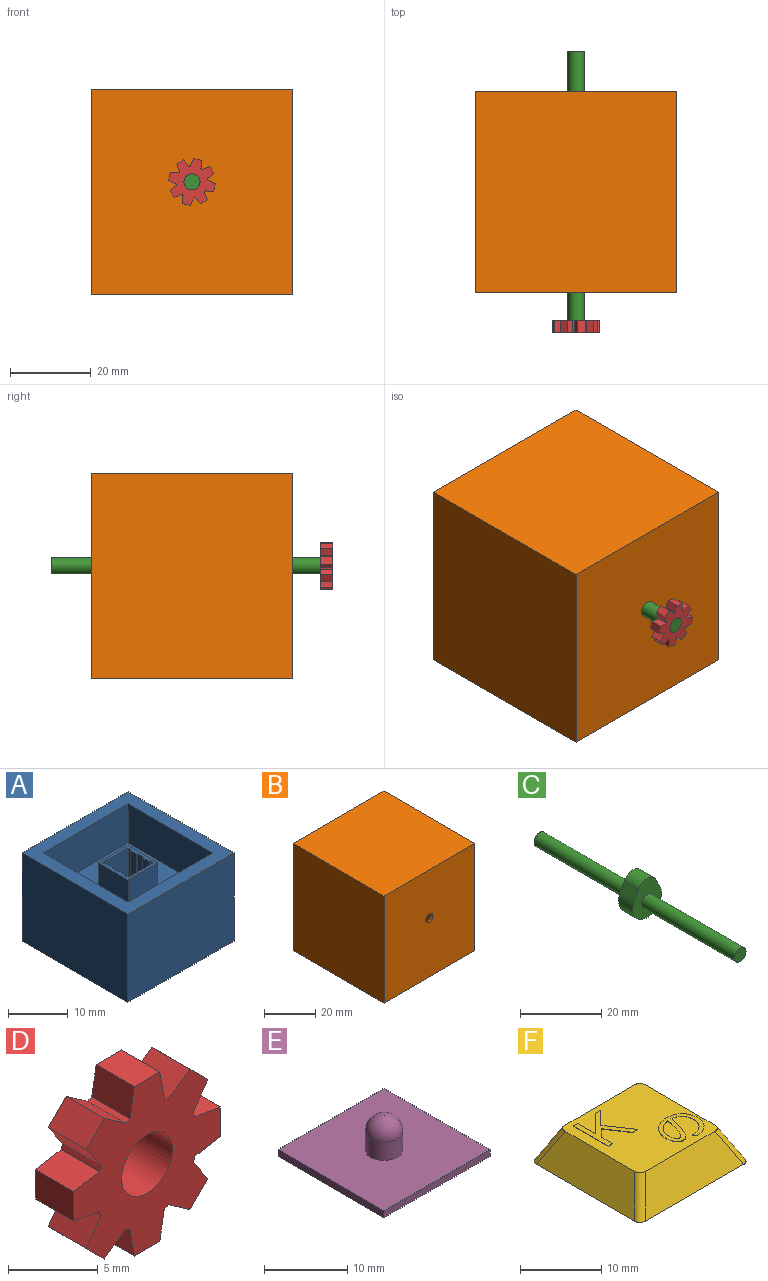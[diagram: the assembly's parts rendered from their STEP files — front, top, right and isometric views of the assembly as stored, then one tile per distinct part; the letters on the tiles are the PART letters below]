
ASSEMBLY  parts=6 mates=6
PART A: 42 faces, bbox 25x25x18 mm
  f0: plane 20x20mm, normal (0,0,1), area 351mm2, adj f1,f2,f3,f4,f32,f33,f34,f35
  f1: plane 7x6mm, normal (0,-1,0), area 42mm2, adj f0,f2,f4,f5
  f2: plane 7x6mm, normal (1,0,0), area 42mm2, adj f0,f1,f3,f5
  f3: plane 7x6mm, normal (0,1,0), area 42mm2, adj f0,f2,f4,f5
  f4: plane 7x6mm, normal (-1,0,0), area 42mm2, adj f0,f1,f3,f5
  f5: plane 7x7mm, normal (0,0,1), area 14.5mm2, adj f1,f2,f3,f4,f6,f7,f8,f9
  f6: plane 7x6mm, normal (0,-1,0), area 42mm2, adj f5,f16,f18,f26
  f7: plane 6x0.25mm, normal (0,-1,0), area 1.5mm2, adj f5,f8,f16,f24
  f8: plane 6x1.5mm, normal (1,0,0), area 9mm2, adj f5,f7,f9,f24
  f9: plane 6x0.25mm, normal (0,1,0), area 1.5mm2, adj f5,f8,f16,f24
  f10: plane 6x0.25mm, normal (0,1,0), area 1.5mm2, adj f5,f11,f18,f23
  f11: plane 6x1.5mm, normal (-1,0,0), area 9mm2, adj f5,f10,f12,f23
  f12: plane 6x0.25mm, normal (0,-1,0), area 1.5mm2, adj f5,f11,f18,f23
  f13: plane 6x0.25mm, normal (0,-1,0), area 1.5mm2, adj f5,f14,f16,f22
  f14: plane 6x1.5mm, normal (1,0,0), area 9mm2, adj f5,f13,f15,f22
  f15: plane 6x0.25mm, normal (0,1,0), area 1.5mm2, adj f5,f14,f16,f22
  f16: plane 7x6mm, normal (1,0,0), area 24mm2, adj f5,f6,f7,f9,f13,f15,f17,f22
  f17: plane 7x6mm, normal (0,1,0), area 42mm2, adj f5,f16,f18,f26
  f18: plane 7x6mm, normal (-1,0,0), area 24mm2, adj f5,f6,f10,f12,f17,f19,f21,f23
  f19: plane 6x0.25mm, normal (0,1,0), area 1.5mm2, adj f5,f18,f20,f25
  f20: plane 6x1.5mm, normal (-1,0,0), area 9mm2, adj f5,f19,f21,f25
  f21: plane 6x0.25mm, normal (0,-1,0), area 1.5mm2, adj f5,f18,f20,f25
  f22: plane 1.5x0.25mm, normal (0,0,-1), area 0.4mm2, adj f13,f14,f15,f16
  f23: plane 1.5x0.25mm, normal (0,0,-1), area 0.4mm2, adj f10,f11,f12,f18
  f24: plane 1.5x0.25mm, normal (0,0,-1), area 0.4mm2, adj f7,f8,f9,f16
  f25: plane 1.5x0.25mm, normal (0,0,-1), area 0.4mm2, adj f18,f19,f20,f21
  f26: plane 20x20mm, normal (0,0,-1), area 364mm2, adj f6,f16,f17,f18,f27,f28,f29,f30
  f27: plane 20x5mm, normal (0,-1,0), area 100mm2, adj f26,f28,f30,f31
  f28: plane 20x5mm, normal (-1,0,0), area 100mm2, adj f26,f27,f29,f31
  f29: plane 20x5mm, normal (0,1,0), area 100mm2, adj f26,f28,f30,f31
  f30: plane 20x5mm, normal (1,0,0), area 100mm2, adj f26,f27,f29,f31
  f31: plane 20x20mm, normal (0,0,1), area 400mm2, adj f27,f28,f29,f30
  f32: plane 20x8mm, normal (-1,0,0), area 160mm2, adj f0,f33,f35,f36
  f33: plane 20x8mm, normal (0,1,0), area 160mm2, adj f0,f32,f34,f36
  f34: plane 20x8mm, normal (1,0,0), area 160mm2, adj f0,f33,f35,f36
  f35: plane 20x8mm, normal (0,-1,0), area 160mm2, adj f0,f32,f34,f36
  f36: plane 25x25mm, normal (0,0,1), area 225mm2, adj f32,f33,f34,f35,f38,f39,f40,f41
  f37: plane 25x25mm, normal (0,0,-1), area 625mm2, adj f38,f39,f40,f41
  f38: plane 25x18mm, normal (-1,0,0), area 450mm2, adj f36,f37,f39,f41
  f39: plane 25x18mm, normal (0,1,0), area 450mm2, adj f36,f37,f38,f40
  f40: plane 25x18mm, normal (1,0,0), area 450mm2, adj f36,f37,f39,f41
  f41: plane 25x18mm, normal (0,-1,0), area 450mm2, adj f36,f37,f38,f40
PART B: 14 faces, bbox 50x50x51 mm
  f0: plane 51x50mm, normal (0,-1,0), area 2537.4mm2, adj f1,f3,f4,f11,f13
  f1: plane 51x50mm, normal (1,0,0), area 2550mm2, adj f0,f2,f4,f13
  f2: plane 51x50mm, normal (0,1,0), area 2537.4mm2, adj f1,f3,f4,f10,f13
  f3: plane 51x50mm, normal (-1,0,0), area 2550mm2, adj f0,f2,f4,f13
  f4: plane 50x50mm, normal (0,0,-1), area 2500mm2, adj f0,f1,f2,f3
  f5: plane 49x48mm, normal (0,1,0), area 2339.4mm2, adj f6,f8,f9,f11,f12
  f6: plane 49x48mm, normal (-1,0,0), area 2352mm2, adj f5,f7,f9,f12
  f7: plane 49x48mm, normal (0,-1,0), area 2339.4mm2, adj f6,f8,f9,f10,f12
  f8: plane 49x48mm, normal (1,0,0), area 2352mm2, adj f5,f7,f9,f12
  f9: plane 48x48mm, normal (0,0,1), area 2304mm2, adj f5,f6,f7,f8
  f10: cylinder r=2mm len=4mm, axis (0,-1,0), area 12.6mm2, adj f2,f7
  f11: cylinder r=2mm len=4mm, axis (0,-1,0), area 12.6mm2, adj f0,f5
  f12: plane 48x48mm, normal (0,0,-1), area 2304mm2, adj f5,f6,f7,f8
  f13: plane 50x50mm, normal (0,0,1), area 2500mm2, adj f0,f1,f2,f3
PART C: 10 faces, bbox 10x70x11.9 mm
  f0: plane 5x2.79mm, normal (0.89,0,0.45), area 15.6mm2, adj f1,f3,f4,f5
  f1: cylinder r=3.43mm len=6.12mm, axis (0,1,0), area 37.8mm2, adj f0,f2,f4,f5
  f2: plane 5x2.79mm, normal (-0.89,0,0.45), area 15.6mm2, adj f1,f3,f4,f5
  f3: cylinder r=5mm len=10mm, axis (0,1,0), area 101.9mm2, adj f0,f2,f4,f5
  f4: plane 11.93x10mm, normal (0,-1,0), area 77.7mm2, adj f0,f1,f2,f3,f8
  f5: plane 11.93x10mm, normal (0,1,0), area 77.7mm2, adj f0,f1,f2,f3,f7
  f6: plane 4x4mm, normal (0,1,0), area 12.6mm2, adj f7
  f7: cylinder r=2mm len=32.5mm, axis (0,1,0), area 408.4mm2, adj f5,f6
  f8: cylinder r=2mm len=32.5mm, axis (0,1,0), area 408.4mm2, adj f4,f9
  f9: plane 4x4mm, normal (0,-1,0), area 12.6mm2, adj f8
PART D: 35 faces, bbox 11.5x3x11.5 mm
  f0: plane 3x1.66mm, normal (-0.57,0,0.82), area 6.1mm2, adj f1,f31,f33,f34
  f1: cylinder r=4mm len=3mm, axis (0,-1,0), area 1.1mm2, adj f0,f2,f33,f34
  f2: plane 3x2mm, normal (0.98,0,0.17), area 6.1mm2, adj f1,f3,f33,f34
  f3: plane 3x2mm, normal (0,0,1), area 6mm2, adj f2,f4,f33,f34
  f4: plane 3x2mm, normal (-0.98,0,0.17), area 6.1mm2, adj f3,f5,f33,f34
  f5: cylinder r=4mm len=3mm, axis (0,-1,0), area 1.1mm2, adj f4,f6,f33,f34
  f6: plane 3x1.66mm, normal (0.57,0,0.82), area 6.1mm2, adj f5,f7,f33,f34
  f7: plane 3x1.41mm, normal (-0.71,0,0.71), area 6mm2, adj f6,f8,f33,f34
  f8: plane 3x1.66mm, normal (-0.82,0,-0.57), area 6.1mm2, adj f7,f9,f33,f34
  f9: cylinder r=4mm len=3mm, axis (0,-1,0), area 1.1mm2, adj f8,f10,f33,f34
  f10: plane 3x2mm, normal (-0.17,0,0.98), area 6.1mm2, adj f9,f11,f33,f34
  f11: plane 3x2mm, normal (-1,0,0), area 6mm2, adj f10,f12,f33,f34
  f12: plane 3x2mm, normal (-0.17,0,-0.98), area 6.1mm2, adj f11,f13,f33,f34
  f13: cylinder r=4mm len=3mm, axis (0,-1,0), area 1.1mm2, adj f12,f14,f33,f34
  f14: plane 3x1.66mm, normal (-0.82,0,0.57), area 6.1mm2, adj f13,f15,f33,f34
  f15: plane 3x1.41mm, normal (-0.71,0,-0.71), area 6mm2, adj f14,f16,f33,f34
  f16: plane 3x1.66mm, normal (0.57,0,-0.82), area 6.1mm2, adj f15,f17,f33,f34
  f17: cylinder r=4mm len=3mm, axis (0,-1,0), area 1.1mm2, adj f16,f18,f33,f34
  f18: plane 3x2mm, normal (-0.98,0,-0.17), area 6.1mm2, adj f17,f19,f33,f34
  f19: plane 3x2mm, normal (0,0,-1), area 6mm2, adj f18,f20,f33,f34
  f20: plane 3x2mm, normal (0.98,0,-0.17), area 6.1mm2, adj f19,f21,f33,f34
  f21: cylinder r=4mm len=3mm, axis (0,-1,0), area 1.1mm2, adj f20,f22,f33,f34
  f22: plane 3x1.66mm, normal (-0.57,0,-0.82), area 6.1mm2, adj f21,f23,f33,f34
  f23: plane 3x1.41mm, normal (0.71,0,-0.71), area 6mm2, adj f22,f24,f33,f34
  f24: plane 3x1.66mm, normal (0.82,0,0.57), area 6.1mm2, adj f23,f25,f33,f34
  f25: cylinder r=4mm len=3mm, axis (0,-1,0), area 1.1mm2, adj f24,f26,f33,f34
  f26: plane 3x2mm, normal (0.17,0,-0.98), area 6.1mm2, adj f25,f27,f33,f34
  f27: plane 3x2mm, normal (1,0,0), area 6mm2, adj f26,f28,f33,f34
  f28: plane 3x2mm, normal (0.17,0,0.98), area 6.1mm2, adj f27,f29,f33,f34
  f29: cylinder r=4mm len=3mm, axis (0,-1,0), area 1.1mm2, adj f28,f30,f33,f34
  f30: plane 3x1.66mm, normal (0.82,0,-0.57), area 6.1mm2, adj f29,f31,f33,f34
  f31: plane 3x1.41mm, normal (0.71,0,0.71), area 6mm2, adj f0,f30,f33,f34
  f32: cylinder r=2mm len=4mm, axis (0,-1,0), area 37.7mm2, adj f33,f34
  f33: plane 11.53x11.53mm, normal (0,1,0), area 71.9mm2, adj f0,f1,f2,f3,f4,f5,f6,f7
  f34: plane 11.53x11.53mm, normal (0,-1,0), area 71.9mm2, adj f0,f1,f2,f3,f4,f5,f6,f7
PART E: 8 faces, bbox 18x18x6 mm
  f0: cylinder r=2.25mm len=4.5mm, axis (0,0,-1), area 38.9mm2, adj f1,f7
  f1: sphere r=2.25mm, area 31.8mm2, adj f0
  f2: plane 18x1mm, normal (1,0,0), area 18mm2, adj f3,f5,f6,f7
  f3: plane 18x1mm, normal (0,1,0), area 18mm2, adj f2,f4,f6,f7
  f4: plane 18x1mm, normal (-1,0,0), area 18mm2, adj f3,f5,f6,f7
  f5: plane 18x1mm, normal (0,-1,0), area 18mm2, adj f2,f4,f6,f7
  f6: plane 18x18mm, normal (0,0,-1), area 324mm2, adj f2,f3,f4,f5
  f7: plane 18x18mm, normal (0,0,1), area 308.1mm2, adj f0,f2,f3,f4,f5
PART F: 76 faces, bbox 19.1x19.1x10.1 mm
  f0: plane 14x14mm, normal (0,0,1), area 168.2mm2, adj f7,f8,f9,f10,f42,f43,f44,f45
  f1: plane 9.5x1.5mm, normal (1,0,0), area 14.2mm2, adj f5,f11,f33,f38
  f2: plane 9.5x0.75mm, normal (1,0,0), area 7.1mm2, adj f5,f11,f16,f35
  f3: plane 9.5x0.75mm, normal (-1,0,0), area 7.1mm2, adj f5,f11,f16,f39
  f4: plane 9.5x1.5mm, normal (-1,0,0), area 14.2mm2, adj f5,f11,f30,f41
  f5: plane 6x6mm, normal (0,0,-1), area 12mm2, adj f1,f2,f3,f4,f16,f17,f18,f19
  f6: plane 19x19mm, normal (0,0,-1), area 40.6mm2, adj f7,f8,f9,f10,f12,f13,f14,f15
  f7: plane 17.21x5mm, normal (0,0.89,0.45), area 82.2mm2, adj f0,f6,f44,f45
  f8: plane 17.21x5mm, normal (-0.89,0,0.45), area 82.2mm2, adj f0,f6,f43,f44
  f9: plane 17.21x5mm, normal (0,-0.89,0.45), area 82.2mm2, adj f0,f6,f42,f43
  f10: plane 17.21x5mm, normal (0.89,0,0.45), area 82.2mm2, adj f0,f6,f42,f45
  f11: plane 13.38x13.38mm, normal (0,0,-1), area 144.6mm2, adj f1,f2,f3,f4,f12,f13,f14,f15
  f12: plane 17.88x4.5mm, normal (0,-0.89,-0.45), area 78.6mm2, adj f6,f11,f13,f15
  f13: plane 17.88x4.5mm, normal (0.89,0,-0.45), area 78.6mm2, adj f6,f11,f12,f14
  f14: plane 17.88x4.5mm, normal (0,0.89,-0.45), area 78.6mm2, adj f6,f11,f13,f15
  f15: plane 17.88x4.5mm, normal (-0.89,0,-0.45), area 78.6mm2, adj f6,f11,f12,f14
  f16: plane 9.5x6mm, normal (0,1,0), area 57mm2, adj f2,f3,f5,f11
  f17: plane 9.5x0.75mm, normal (1,0,0), area 7.1mm2, adj f5,f11,f18,f36
  f18: plane 9.5x6mm, normal (0,-1,0), area 57mm2, adj f5,f11,f17,f19
  f19: plane 9.5x0.75mm, normal (-1,0,0), area 7.1mm2, adj f5,f11,f18,f32
  f20: plane 9.5x2.25mm, normal (0,-1,0), area 21.4mm2, adj f5,f21,f23,f24
  f21: plane 9.5x5mm, normal (-1,0,0), area 47.5mm2, adj f5,f20,f22,f24
  f22: plane 9.5x2.25mm, normal (0,1,0), area 21.4mm2, adj f5,f21,f23,f24
  f23: plane 9.5x5mm, normal (1,0,0), area 47.5mm2, adj f5,f20,f22,f24
  f24: plane 5x2.25mm, normal (0,0,-1), area 11.2mm2, adj f20,f21,f22,f23
  f25: plane 9.5x5mm, normal (1,0,0), area 47.5mm2, adj f5,f26,f28,f29
  f26: plane 9.5x2.25mm, normal (0,-1,0), area 21.4mm2, adj f5,f25,f27,f29
  f27: plane 9.5x5mm, normal (-1,0,0), area 47.5mm2, adj f5,f26,f28,f29
  f28: plane 9.5x2.25mm, normal (0,1,0), area 21.4mm2, adj f5,f25,f27,f29
  f29: plane 5x2.25mm, normal (0,0,-1), area 11.2mm2, adj f25,f26,f27,f28
  f30: plane 9.5x0.25mm, normal (0,-1,0), area 2.4mm2, adj f4,f5,f11,f31
  f31: plane 9.5x1.5mm, normal (-1,0,0), area 14.2mm2, adj f5,f11,f30,f32
  f32: plane 9.5x0.25mm, normal (0,1,0), area 2.4mm2, adj f5,f11,f19,f31
  f33: plane 9.5x0.25mm, normal (0,1,0), area 2.4mm2, adj f1,f5,f11,f34
  f34: plane 9.5x1.5mm, normal (1,0,0), area 14.2mm2, adj f5,f11,f33,f35
  f35: plane 9.5x0.25mm, normal (0,-1,0), area 2.4mm2, adj f2,f5,f11,f34
  f36: plane 9.5x0.25mm, normal (0,1,0), area 2.4mm2, adj f5,f11,f17,f37
  f37: plane 9.5x1.5mm, normal (1,0,0), area 14.2mm2, adj f5,f11,f36,f38
  f38: plane 9.5x0.25mm, normal (0,-1,0), area 2.4mm2, adj f1,f5,f11,f37
  f39: plane 9.5x0.25mm, normal (0,-1,0), area 2.4mm2, adj f3,f5,f11,f40
  f40: plane 9.5x1.5mm, normal (-1,0,0), area 14.2mm2, adj f5,f11,f39,f41
  f41: plane 9.5x0.25mm, normal (0,1,0), area 2.4mm2, adj f4,f5,f11,f40
  f42: cylinder r=1mm len=5.26mm, axis (-0.41,0.41,0.82), area 8.4mm2, adj f0,f6,f9,f10
  f43: cylinder r=1mm len=5.26mm, axis (-0.41,-0.41,-0.82), area 8.4mm2, adj f0,f6,f8,f9
  f44: cylinder r=1mm len=5.26mm, axis (0.41,-0.41,0.82), area 8.4mm2, adj f0,f6,f7,f8
  f45: cylinder r=1mm len=5.26mm, axis (0.41,0.41,-0.82), area 8.4mm2, adj f0,f6,f7,f10
  f46: plane 6.13x0.05mm, normal (-1,0,0), area 0.3mm2, adj f0,f47,f50,f59
  f47: plane 0.77x0.05mm, normal (0,-1,0), area 0mm2, adj f0,f46,f51,f59
  f48: plane 0.88x0.05mm, normal (0,-1,0), area 0mm2, adj f0,f53,f54,f59
  f49: plane 0.89x0.05mm, normal (0,1,0), area 0mm2, adj f0,f55,f56,f59
  f50: plane 0.77x0.05mm, normal (0,1,0), area 0mm2, adj f0,f46,f58,f59
  f51: plane 1.92x0.05mm, normal (1,0,0), area 0.1mm2, adj f0,f47,f52,f59
  f52: plane 1.32x1.28mm, normal (0.72,-0.7,0), area 0.1mm2, adj f0,f51,f53,f59
  f53: plane 3.23x2.16mm, normal (-0.83,-0.56,0), area 0.2mm2, adj f0,f48,f52,f59
  f54: plane 3.78x2.56mm, normal (0.83,0.56,0), area 0.2mm2, adj f0,f48,f55,f59
  f55: plane 2.34x2.22mm, normal (0.73,-0.69,0), area 0.2mm2, adj f0,f49,f54,f59
  f56: plane 3.14x3.05mm, normal (-0.72,0.7,0), area 0.2mm2, adj f0,f49,f57,f59
  f57: plane 0.05x0.03mm, normal (0,1,0), area 0mm2, adj f0,f56,f58,f59
  f58: plane 3.14x0.05mm, normal (1,0,0), area 0.2mm2, adj f0,f50,f57,f59
  f59: plane 6.13x5.08mm, normal (0,0,1), area 11.2mm2, adj f46,f47,f48,f49,f50,f51,f52,f53
  f60: extruded ~2.77x2.65mm, area 0.2mm2, adj f0,f61,f68,f74
  f61: extruded ~3.16x2.94mm, area 0.2mm2, adj f0,f60,f62,f74
  f62: extruded ~1.93x1.29mm, area 0.1mm2, adj f0,f61,f63,f74
  f63: extruded ~2.24x1.69mm, area 0.1mm2, adj f0,f62,f69,f74
  f64: extruded ~1.7x1.09mm, area 0.1mm2, adj f65,f73,f74,f75
  f65: extruded ~1.31x0.74mm, area 0.1mm2, adj f64,f66,f74,f75
  f66: extruded ~2.33x2.23mm, area 0.2mm2, adj f65,f73,f74,f75
  f67: plane 0.55x0.34mm, normal (-0.85,-0.52,0), area 0mm2, adj f0,f68,f72,f74
  f68: extruded ~2.75x2.72mm, area 0.2mm2, adj f0,f60,f67,f74
  f69: extruded ~2.08x0.43mm, area 0.1mm2, adj f0,f63,f70,f74
  f70: extruded ~2.09x1.92mm, area 0.2mm2, adj f0,f69,f71,f74
  f71: extruded ~2.14x1.83mm, area 0.2mm2, adj f0,f70,f72,f74
  f72: extruded ~0.62x0.09mm, area 0mm2, adj f0,f67,f71,f74
  f73: extruded ~1.95x0.4mm, area 0.1mm2, adj f64,f66,f74,f75
  f74: plane 5.93x5.4mm, normal (0,0,1), area 11mm2, adj f60,f61,f62,f63,f64,f65,f66,f67
  f75: plane 3.64x2.23mm, normal (0,0,1), area 5mm2, adj f64,f65,f66,f73
PLACE A rot(axis=(-0.01,0.7,-0.71),0deg) t=(-37.27,-50.85,-43.99)mm
PLACE B t=(-37.27,-50.85,-43.99)mm fixed
PLACE C rot(axis=(0,-1,0),75.9deg) t=(-43.62,-50.85,-97.41)mm
PLACE D rot(axis=(0,-1,0),75.9deg) t=(-43.62,-50.85,-97.41)mm
PLACE E t=(-37.27,-50.85,-43.99)mm
PLACE F rot(axis=(0.02,0.48,-0.88),0deg) t=(-37.27,-50.85,-45.04)mm
MATE fastened D.f1 <-> C.f3  axis (0,-1,0) through (-37.27,-85.85,-34.99)mm
MATE revolute C.f3 <-> B.f10  axis (0,-1,0) through (-37.27,-85.85,-34.99)mm
MATE fastened E.f0 <-> A.f31  axis (0,0,-1) through (-37.27,-50.85,-57.99)mm
MATE slider F.f5 <-> E.f0  axis (0,0,-1) through (-37.27,-50.85,-50.04)mm
MATE revolute C.f3 <-> B.f10  axis (0,-1,0) through (-37.27,-85.85,-34.99)mm
MATE fastened B.f9 <-> A.f37  axis (0,0,1) through (-37.27,-50.85,-61.99)mm
